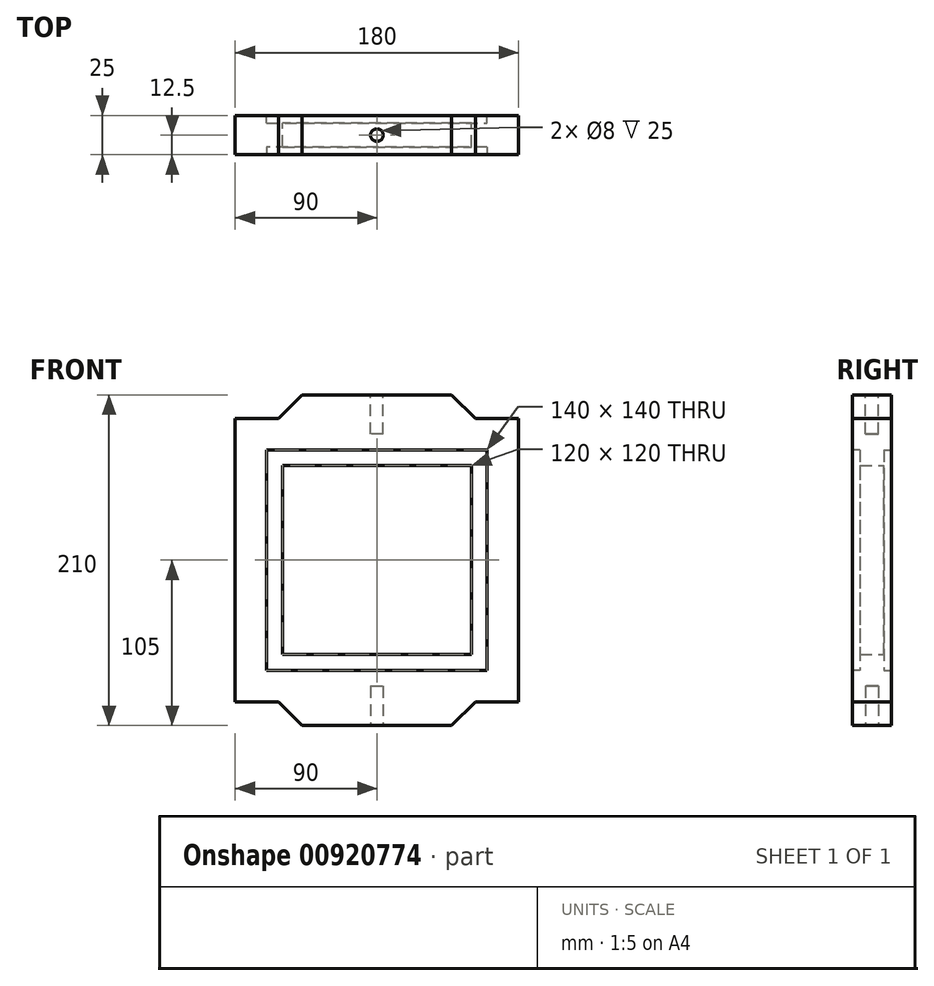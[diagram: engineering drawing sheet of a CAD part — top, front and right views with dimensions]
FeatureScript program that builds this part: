
annotation { "Feature Type Name" : "Feature", "Feature Type Description" : "" }
export const myFeature = defineFeature(function(context is Context, id is Id, definition is map)
    precondition{}
    {
        {
            var Q0;
            Q0=qCreatedBy(makeId("Front.planeOp"),FACE);
            var sketch = newSketch(context, id + "F0", { "sketchPlane" : qUnion([Q0])});
            skLineSegment(sketch, "E0.bottom", {"start": v(90, 90) * mm, "end": v(-90, 90) * mm});
            skLineSegment(sketch, "E0.top", {"start": v(90, -90) * mm, "end": v(-90, -90) * mm});
            skLineSegment(sketch, "E0.left", {"start": v(90, 90) * mm, "end": v(90, -90) * mm});
            skLineSegment(sketch, "E0.right", {"start": v(-90, 90) * mm, "end": v(-90, -90) * mm});
            skPoint(sketch, "E0.middle", {"position": v(0, 0) * mm});
            skSolve(sketch);
        }
        {
            var Q0;
            Q0 = qSketchRegion(id + "F0", true);
            extrude(context, id + "F1", {"entities" : qUnion([Q0]), "depth" : 25 * mm, "offsetDistance" : 25 * mm});
        }
        {
            var Q0;
            Q0=makeQuery(id+"F1.opExtrude","SWEPT_FACE",FACE,{"disambiguationData":[OSD([sQuery(id+"F0.wireOp",EDGE,"E0.top")])]});
            var sketch = newSketch(context, id + "F2", { "sketchPlane" : qUnion([Q0])});
            skLineSegment(sketch, "E1", {"start": v(0, 25) * mm, "end": v(0, 0) * mm, "construction": true});
            skLineSegment(sketch, "E2.bottom", {"start": v(62.5, 25) * mm, "end": v(-62.5, 25) * mm});
            skLineSegment(sketch, "E2.top", {"start": v(62.5, 0) * mm, "end": v(-62.5, 0) * mm});
            skLineSegment(sketch, "E2.left", {"start": v(62.5, 25) * mm, "end": v(62.5, 0) * mm});
            skLineSegment(sketch, "E2.right", {"start": v(-62.5, 25) * mm, "end": v(-62.5, 0) * mm});
            skPoint(sketch, "E2.middle", {"position": v(0, 12.5) * mm});
            skSolve(sketch);
        }
        {
            var Q0;
            Q0 = qSketchRegion(id + "F2", true);
            extrude(context, id + "F3", {"entities" : qUnion([Q0]), "operationType" : NewBodyOperationType.ADD, "depth" : 15 * mm, "offsetDistance" : 25 * mm});
        }
        {
            var Q0;
            Q0=makeQuery(id+"F1.opExtrude","SWEPT_FACE",FACE,{"disambiguationData":[OSD([sQuery(id+"F0.wireOp",EDGE,"E0.bottom")])]});
            var sketch = newSketch(context, id + "F4", { "sketchPlane" : qUnion([Q0])});
            skLineSegment(sketch, "E3", {"start": v(0, -25) * mm, "end": v(0, 0) * mm, "construction": true});
            skLineSegment(sketch, "E4.bottom", {"start": v(62.5, 0) * mm, "end": v(-62.5, 0) * mm});
            skLineSegment(sketch, "E4.top", {"start": v(62.5, -25) * mm, "end": v(-62.5, -25) * mm});
            skLineSegment(sketch, "E4.left", {"start": v(62.5, 0) * mm, "end": v(62.5, -25) * mm});
            skLineSegment(sketch, "E4.right", {"start": v(-62.5, 0) * mm, "end": v(-62.5, -25) * mm});
            skPoint(sketch, "E4.middle", {"position": v(0, -12.5) * mm});
            skSolve(sketch);
        }
        {
            var Q0;
            Q0 = qSketchRegion(id + "F4", true);
            extrude(context, id + "F5", {"entities" : qUnion([Q0]), "operationType" : NewBodyOperationType.ADD, "depth" : (15) * mm, "offsetDistance" : 25 * mm});
        }
        {
            var Q0;
            Q0=makeQuery(id+"F5.boolean.opBoolean","MERGE",FACE,{"derivedFrom":[makeQuery(id+"F3.boolean.opBoolean","MERGE",FACE,{"derivedFrom":[makeQuery(id+"F1.opExtrude","CAP_FACE",FACE,{"disambiguationData":[OSD([sQuery(id+"F0.wireOp",EDGE,"E0.bottom"),sQuery(id+"F0.wireOp",EDGE,"E0.top"),sQuery(id+"F0.wireOp",EDGE,"E0.left"),sQuery(id+"F0.wireOp",EDGE,"E0.right")])],"isStart":false}),makeQuery(id+"F3.opExtrude","SWEPT_FACE",FACE,{"disambiguationData":[OSD([sQuery(id+"F2.wireOp",EDGE,"E2.bottom")])]})]}),makeQuery(id+"F5.opExtrude","SWEPT_FACE",FACE,{"disambiguationData":[OSD([sQuery(id+"F4.wireOp",EDGE,"E4.top")])]})]});
            var sketch = newSketch(context, id + "F6", { "sketchPlane" : qUnion([Q0])});
            skLineSegment(sketch, "E5", {"start": v(-62.5, -90) * mm, "end": v(-47.5, -105) * mm});
            skLineSegment(sketch, "E6", {"start": v(-47.5, -105) * mm, "end": v(-62.5, -105) * mm});
            skLineSegment(sketch, "E7", {"start": v(-62.5, -105) * mm, "end": v(-62.5, -90) * mm});
            skLineSegment(sketch, "E8", {"start": v(62.5, -90) * mm, "end": v(47.5, -105) * mm});
            skLineSegment(sketch, "E9", {"start": v(47.5, -105) * mm, "end": v(62.5, -105) * mm});
            skLineSegment(sketch, "E10", {"start": v(62.5, -105) * mm, "end": v(62.5, -90) * mm});
            skLineSegment(sketch, "E11", {"start": v(-62.5, 90) * mm, "end": v(-47.5, 105) * mm});
            skLineSegment(sketch, "E12", {"start": v(-47.5, 105) * mm, "end": v(-62.5, 105) * mm});
            skLineSegment(sketch, "E13", {"start": v(-62.5, 105) * mm, "end": v(-62.5, 90) * mm});
            skLineSegment(sketch, "E14", {"start": v(62.5, 90) * mm, "end": v(47.5, 105) * mm});
            skLineSegment(sketch, "E15", {"start": v(47.5, 105) * mm, "end": v(62.5, 105) * mm});
            skLineSegment(sketch, "E16", {"start": v(62.5, 105) * mm, "end": v(62.5, 90) * mm});
            skSolve(sketch);
        }
        {
            var Q0;
            Q0 = qSketchRegion(id + "F6", true);
            extrude(context, id + "F7", {"entities" : qUnion([Q0]), "operationType" : NewBodyOperationType.REMOVE, "oppositeDirection" : true, "depth" : 25 * mm, "offsetDistance" : 25 * mm});
        }
        {
            var Q0;
            Q0=makeQuery(id+"F5.boolean.opBoolean","MERGE",FACE,{"derivedFrom":[makeQuery(id+"F3.boolean.opBoolean","MERGE",FACE,{"derivedFrom":[makeQuery(id+"F1.opExtrude","CAP_FACE",FACE,{"disambiguationData":[OSD([sQuery(id+"F0.wireOp",EDGE,"E0.bottom"),sQuery(id+"F0.wireOp",EDGE,"E0.top"),sQuery(id+"F0.wireOp",EDGE,"E0.left"),sQuery(id+"F0.wireOp",EDGE,"E0.right")])],"isStart":true}),makeQuery(id+"F3.opExtrude","SWEPT_FACE",FACE,{"disambiguationData":[OSD([sQuery(id+"F2.wireOp",EDGE,"E2.top")])]})]}),makeQuery(id+"F5.opExtrude","SWEPT_FACE",FACE,{"disambiguationData":[OSD([sQuery(id+"F4.wireOp",EDGE,"E4.bottom")])]})]});
            var sketch = newSketch(context, id + "F8", { "sketchPlane" : qUnion([Q0])});
            skLineSegment(sketch, "E17.bottom", {"start": v(60, 60) * mm, "end": v(-60, 60) * mm});
            skLineSegment(sketch, "E17.top", {"start": v(60, -60) * mm, "end": v(-60, -60) * mm});
            skLineSegment(sketch, "E17.left", {"start": v(60, 60) * mm, "end": v(60, -60) * mm});
            skLineSegment(sketch, "E17.right", {"start": v(-60, 60) * mm, "end": v(-60, -60) * mm});
            skPoint(sketch, "E17.middle", {"position": v(0, 0) * mm});
            skSolve(sketch);
        }
        {
            var Q0;
            Q0 = qSketchRegion(id + "F8", true);
            extrude(context, id + "F9", {"entities" : qUnion([Q0]), "operationType" : NewBodyOperationType.REMOVE, "oppositeDirection" : true, "depth" : 25 * mm, "offsetDistance" : 25 * mm});
        }
        {
            var Q0;
            Q0=makeQuery(id+"F5.boolean.opBoolean","MERGE",FACE,{"derivedFrom":[makeQuery(id+"F3.boolean.opBoolean","MERGE",FACE,{"derivedFrom":[makeQuery(id+"F1.opExtrude","CAP_FACE",FACE,{"disambiguationData":[OSD([sQuery(id+"F0.wireOp",EDGE,"E0.bottom"),sQuery(id+"F0.wireOp",EDGE,"E0.top"),sQuery(id+"F0.wireOp",EDGE,"E0.left"),sQuery(id+"F0.wireOp",EDGE,"E0.right")])],"isStart":true}),makeQuery(id+"F3.opExtrude","SWEPT_FACE",FACE,{"disambiguationData":[OSD([sQuery(id+"F2.wireOp",EDGE,"E2.top")])]})]}),makeQuery(id+"F5.opExtrude","SWEPT_FACE",FACE,{"disambiguationData":[OSD([sQuery(id+"F4.wireOp",EDGE,"E4.bottom")])]})]});
            var sketch = newSketch(context, id + "F10", { "sketchPlane" : qUnion([Q0])});
            skLineSegment(sketch, "E18.bottom", {"start": v(70, 70) * mm, "end": v(-70, 70) * mm});
            skLineSegment(sketch, "E18.top", {"start": v(70, -70) * mm, "end": v(-70, -70) * mm});
            skLineSegment(sketch, "E18.left", {"start": v(70, 70) * mm, "end": v(70, -70) * mm});
            skLineSegment(sketch, "E18.right", {"start": v(-70, 70) * mm, "end": v(-70, -70) * mm});
            skPoint(sketch, "E18.middle", {"position": v(0, 0) * mm});
            skSolve(sketch);
        }
        {
            var Q0;
            Q0 = qSketchRegion(id + "F10", true);
            extrude(context, id + "F11", {"entities" : qUnion([Q0]), "operationType" : NewBodyOperationType.REMOVE, "oppositeDirection" : true, "depth" : 5 * mm, "offsetDistance" : 25 * mm});
        }
        {
            var Q0;
            Q0=makeQuery(id+"F5.boolean.opBoolean","MERGE",FACE,{"derivedFrom":[makeQuery(id+"F3.boolean.opBoolean","MERGE",FACE,{"derivedFrom":[makeQuery(id+"F1.opExtrude","CAP_FACE",FACE,{"disambiguationData":[OSD([sQuery(id+"F0.wireOp",EDGE,"E0.bottom"),sQuery(id+"F0.wireOp",EDGE,"E0.top"),sQuery(id+"F0.wireOp",EDGE,"E0.left"),sQuery(id+"F0.wireOp",EDGE,"E0.right")])],"isStart":false}),makeQuery(id+"F3.opExtrude","SWEPT_FACE",FACE,{"disambiguationData":[OSD([sQuery(id+"F2.wireOp",EDGE,"E2.bottom")])]})]}),makeQuery(id+"F5.opExtrude","SWEPT_FACE",FACE,{"disambiguationData":[OSD([sQuery(id+"F4.wireOp",EDGE,"E4.top")])]})]});
            var sketch = newSketch(context, id + "F12", { "sketchPlane" : qUnion([Q0])});
            skLineSegment(sketch, "E19.bottom", {"start": v(70, 70) * mm, "end": v(-70, 70) * mm});
            skLineSegment(sketch, "E19.top", {"start": v(70, -70) * mm, "end": v(-70, -70) * mm});
            skLineSegment(sketch, "E19.left", {"start": v(70, 70) * mm, "end": v(70, -70) * mm});
            skLineSegment(sketch, "E19.right", {"start": v(-70, 70) * mm, "end": v(-70, -70) * mm});
            skPoint(sketch, "E19.middle", {"position": v(0, 0) * mm});
            skSolve(sketch);
        }
        {
            var Q0;
            Q0 = qSketchRegion(id + "F12", true);
            extrude(context, id + "F13", {"entities" : qUnion([Q0]), "operationType" : NewBodyOperationType.REMOVE, "oppositeDirection" : true, "depth" : 5 * mm, "offsetDistance" : 25 * mm});
        }
        {
            var Q0;
            Q0=makeQuery(id+"F3.opExtrude","CAP_FACE",FACE,{"disambiguationData":[OSD([sQuery(id+"F2.wireOp",EDGE,"E2.bottom"),sQuery(id+"F2.wireOp",EDGE,"E2.top"),sQuery(id+"F2.wireOp",EDGE,"E2.left"),sQuery(id+"F2.wireOp",EDGE,"E2.right")])],"isStart":false});
            var sketch = newSketch(context, id + "F14", { "sketchPlane" : qUnion([Q0])});
            skLineSegment(sketch, "E20", {"start": v(-47.5, 25) * mm, "end": v(47.5, 0) * mm, "construction": true});
            skCircle(sketch, "E21", {"center": v(0, 12.5) * mm, "radius": 4 * mm});
            skSolve(sketch);
        }
        {
            var Q0;
            Q0 = qSketchRegion(id + "F14", true);
            extrude(context, id + "F15", {"entities" : qUnion([Q0]), "operationType" : NewBodyOperationType.REMOVE, "oppositeDirection" : true, "depth" : 25 * mm, "offsetDistance" : 25 * mm});
        }
        {
            var Q0;
            Q0=makeQuery(id+"F5.opExtrude","CAP_FACE",FACE,{"disambiguationData":[OSD([sQuery(id+"F4.wireOp",EDGE,"E4.bottom"),sQuery(id+"F4.wireOp",EDGE,"E4.top"),sQuery(id+"F4.wireOp",EDGE,"E4.left"),sQuery(id+"F4.wireOp",EDGE,"E4.right")])],"isStart":false});
            var sketch = newSketch(context, id + "F16", { "sketchPlane" : qUnion([Q0])});
            skLineSegment(sketch, "E22", {"start": v(-47.5, 0) * mm, "end": v(47.5, -25) * mm, "construction": true});
            skCircle(sketch, "E23", {"center": v(0, -12.5) * mm, "radius": 4 * mm});
            skSolve(sketch);
        }
        {
            var Q0;
            Q0 = qSketchRegion(id + "F16", true);
            extrude(context, id + "F17", {"entities" : qUnion([Q0]), "operationType" : NewBodyOperationType.REMOVE, "oppositeDirection" : true, "depth" : 25 * mm, "offsetDistance" : 25 * mm});
        }
    });
